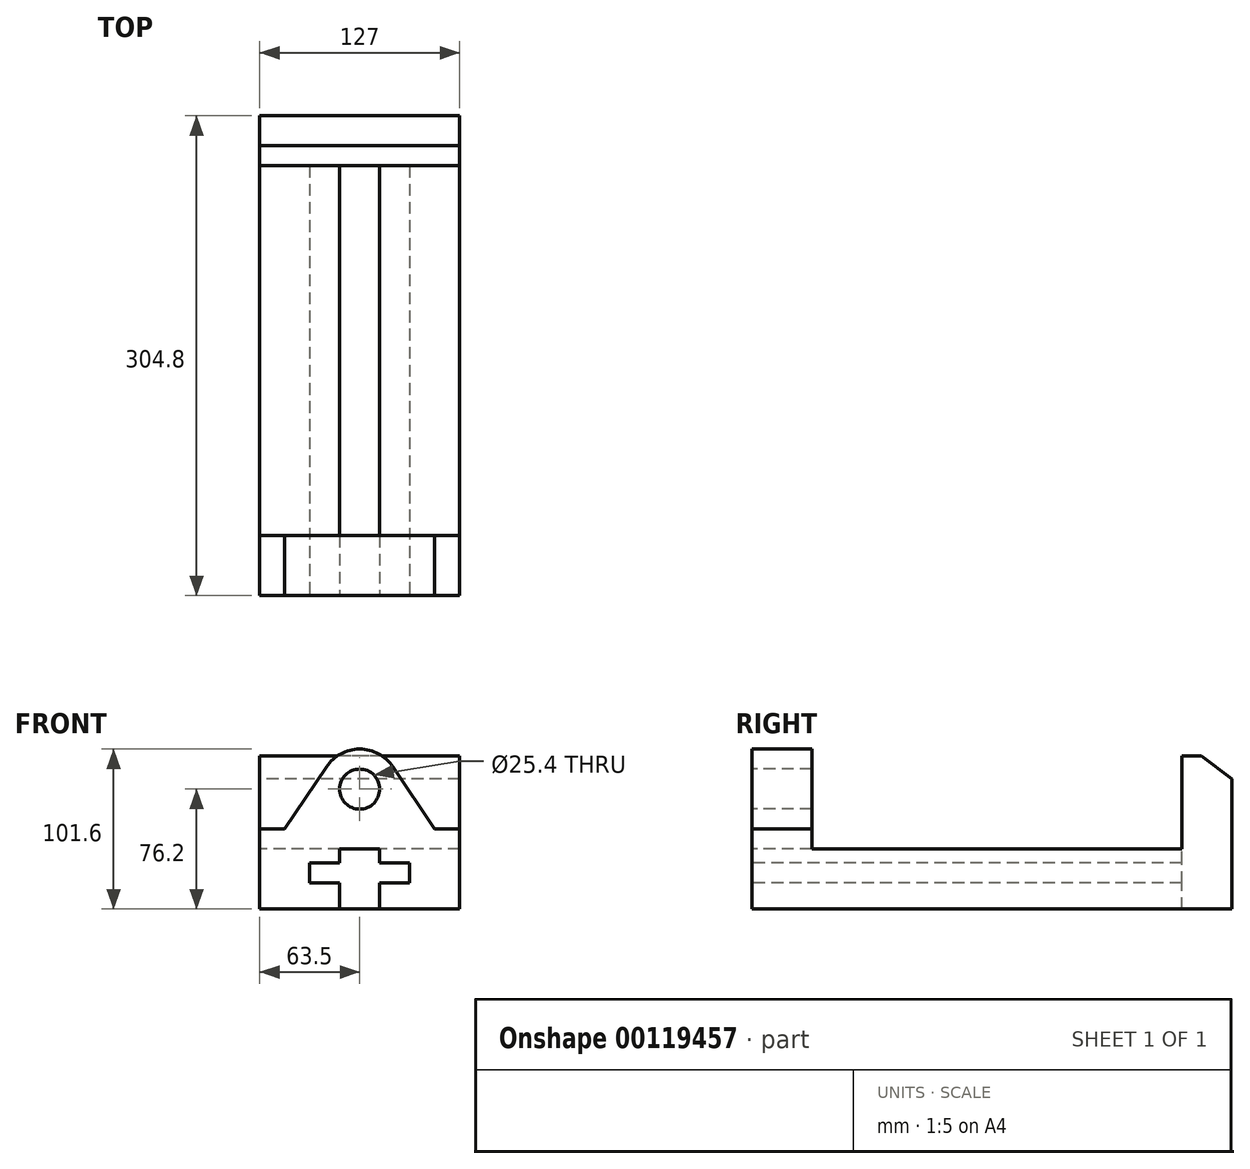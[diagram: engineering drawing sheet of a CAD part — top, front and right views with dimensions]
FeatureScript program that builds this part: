
annotation { "Feature Type Name" : "Feature", "Feature Type Description" : "" }
export const myFeature = defineFeature(function(context is Context, id is Id, definition is map)
    precondition{}
    {
        {
            var Q0;
            Q0=qCreatedBy(makeId("Front.planeOp"),FACE);
            var sketch = newSketch(context, id + "F0", { "sketchPlane" : qUnion([Q0])});
            skLineSegment(sketch, "E0.left", {"start": v(-12.7, 0) * mm, "end": v(-12.7, 16.51) * mm});
            skLineSegment(sketch, "E0.right", {"start": v(12.7, 0) * mm, "end": v(12.7, 16.51) * mm});
            skLineSegment(sketch, "E1", {"start": v(-12.7, 16.51) * mm, "end": v(-31.75, 16.51) * mm});
            skLineSegment(sketch, "E2", {"start": v(-31.75, 16.51) * mm, "end": v(-31.75, 29.21) * mm});
            skLineSegment(sketch, "E3", {"start": v(-31.75, 29.21) * mm, "end": v(-12.7, 29.21) * mm});
            skLineSegment(sketch, "E4", {"start": v(-12.7, 29.21) * mm, "end": v(-12.7, 38.1) * mm});
            skLineSegment(sketch, "E5", {"start": v(-12.7, 38.1) * mm, "end": v(12.7, 38.1) * mm});
            skLineSegment(sketch, "E6", {"start": v(12.7, 38.1) * mm, "end": v(12.7, 29.21) * mm});
            skLineSegment(sketch, "E7", {"start": v(12.7, 29.21) * mm, "end": v(31.75, 29.21) * mm});
            skLineSegment(sketch, "E8", {"start": v(31.75, 29.21) * mm, "end": v(31.75, 16.51) * mm});
            skLineSegment(sketch, "E9", {"start": v(31.75, 16.51) * mm, "end": v(12.7, 16.51) * mm});
            skLineSegment(sketch, "E10", {"start": v(-12.7, 0) * mm, "end": v(-63.5, 0) * mm});
            skLineSegment(sketch, "E11", {"start": v(12.7, 0) * mm, "end": v(63.5, 0) * mm});
            skLineSegment(sketch, "E12", {"start": v(-129.82, 0) * mm, "end": v(-129.82, 85.1) * mm, "construction": true});
            skLineSegment(sketch, "E13", {"start": v(-63.5, 0) * mm, "end": v(-63.5, 50.8) * mm});
            skLineSegment(sketch, "E14", {"start": v(-63.5, 50.8) * mm, "end": v(-47.62, 50.8) * mm});
            skLineSegment(sketch, "E15", {"start": v(0, 175.9) * mm, "end": v(0, -52.31) * mm, "construction": true});
            skLineSegment(sketch, "E16.MirrorCS", {"start": v(63.5, 50.8) * mm, "end": v(47.62, 50.8) * mm});
            skLineSegment(sketch, "E17.MirrorCS", {"start": v(63.5, 0) * mm, "end": v(63.5, 50.8) * mm});
            skPoint(sketch, "E18.visualSharp", {"position": v(0, 170.12) * mm});
            skLineSegment(sketch, "E19", {"start": v(-12.7, 0) * mm, "end": v(12.7, 0) * mm});
            skCircle(sketch, "E20", {"center": v(0, 76.2) * mm, "radius": 12.7 * mm});
            skLineSegment(sketch, "E21", {"start": v(-47.63, 50.8) * mm, "end": v(-21.1, 90.35) * mm});
            skLineSegment(sketch, "E22.MirrorCS", {"start": v(47.63, 50.8) * mm, "end": v(21.1, 90.35) * mm});
            skArc(sketch, "E23", {"start": v(-21.1, 90.35) * mm, "mid": v(0, 101.6) * mm, "end": v(21.1, 90.35) * mm});
            skLineSegment(sketch, "E24", {"start": v(-63.5, 50.8) * mm, "end": v(-63.5, 101.6) * mm});
            skPoint(sketch, "E24.endSnap0", {"position": v(0, 101.6) * mm});
            skLineSegment(sketch, "E25", {"start": v(-63.5, 101.6) * mm, "end": v(63.5, 101.6) * mm});
            skLineSegment(sketch, "E26", {"start": v(63.5, 101.6) * mm, "end": v(63.5, 50.8) * mm});
            skSolve(sketch);
        }
        {
            var Q0;
            Q0=qCreatedBy(makeId("Right.planeOp"),FACE);
            var sketch = newSketch(context, id + "F1", { "sketchPlane" : qUnion([Q0])});
            skLineSegment(sketch, "E27", {"start": v(0, 0) * mm, "end": v(304.8, 0) * mm});
            skLineSegment(sketch, "E28", {"start": v(304.8, 0) * mm, "end": v(304.8, 82.55) * mm});
            skLineSegment(sketch, "E29", {"start": v(304.8, 82.55) * mm, "end": v(285.75, 97.3) * mm});
            skLineSegment(sketch, "E30", {"start": v(285.75, 97.3) * mm, "end": v(273.05, 97.3) * mm});
            skLineSegment(sketch, "E31", {"start": v(273.05, 97.3) * mm, "end": v(273.05, 38.1) * mm});
            skLineSegment(sketch, "E32", {"start": v(273.05, 38.1) * mm, "end": v(38.1, 38.1) * mm});
            skLineSegment(sketch, "E33", {"start": v(38.1, 38.1) * mm, "end": v(38.1, 101.6) * mm});
            skLineSegment(sketch, "E34", {"start": v(38.1, 101.6) * mm, "end": v(0, 101.6) * mm});
            skLineSegment(sketch, "E35", {"start": v(0, 101.6) * mm, "end": v(0, 0) * mm});
            skSolve(sketch);
        }
        {
            var Q0;
            Q0=makeQuery(id+"F1.imprint","IMPRINT",FACE,{"disambiguationData":[TD([[makeQuery(id+"F1.imprint","IMPRINT",EDGE,{"derivedFrom":sQuery(id+"F1.wireOp",EDGE,"E27")}),1.0]])]});
            extrude(context, id + "F2", {"entities" : qUnion([Q0]), "endBound" : BoundingType.SYMMETRIC, "depth" : 127 * mm});
        }
        {
            var Q0;
            Q0=makeQuery(id+"F0.imprint","IMPRINT",FACE,{"disambiguationData":[TD([[makeQuery(id+"F0.imprint","IMPRINT",EDGE,{"derivedFrom":sQuery(id+"F0.wireOp",EDGE,"E0.left")}),-1.0]])]});
            extrude(context, id + "F3", {"entities" : qUnion([Q0]), "operationType" : NewBodyOperationType.REMOVE, "oppositeDirection" : true, "depth" : 273.05 * mm});
        }
        {
            var Q0;
            Q0=makeQuery(id+"F0.imprint","IMPRINT",FACE,{"disambiguationData":[TD([[makeQuery(id+"F0.imprint","IMPRINT",EDGE,{"derivedFrom":sQuery(id+"F0.wireOp",EDGE,"E14")}),1.0]])]});
            var Q1;
            Q1=makeQuery(id+"F0.imprint","IMPRINT",FACE,{"disambiguationData":[TD([[makeQuery(id+"F0.imprint","IMPRINT",EDGE,{"derivedFrom":sQuery(id+"F0.wireOp",EDGE,"E16.MirrorCS")}),-1.0]])]});
            var Q2;
            Q2=makeQuery(id+"F0.imprint","IMPRINT",FACE,{"disambiguationData":[TD([[makeQuery(id+"F0.imprint","IMPRINT",EDGE,{"derivedFrom":sQuery(id+"F0.wireOp",EDGE,"E20")}),1.0]])]});
            extrude(context, id + "F4", {"entities" : qUnion([Q0, Q1, Q2]), "operationType" : NewBodyOperationType.REMOVE, "oppositeDirection" : true, "depth" : 38.1 * mm});
        }
    });
